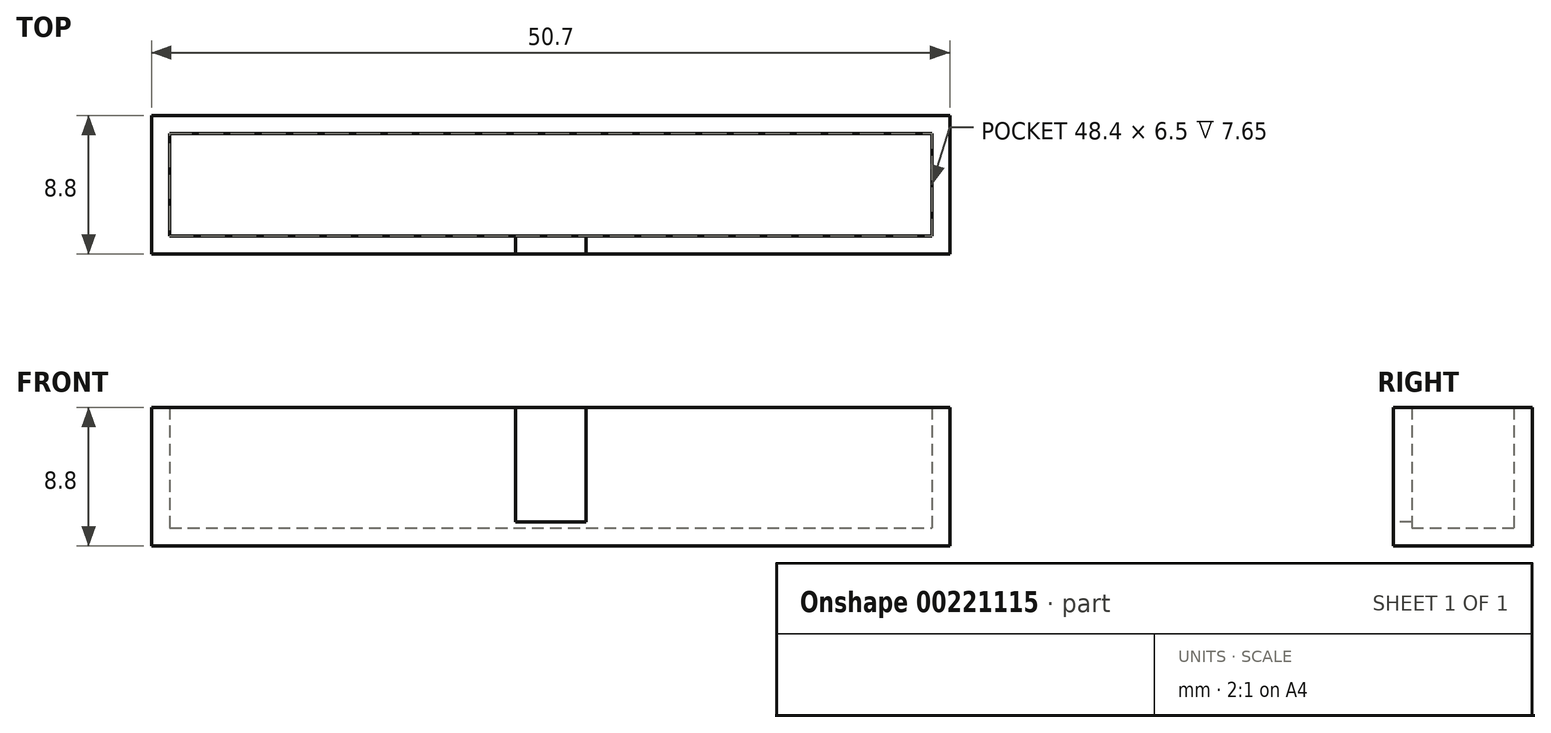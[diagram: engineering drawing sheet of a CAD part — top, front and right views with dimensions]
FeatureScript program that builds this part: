
annotation { "Feature Type Name" : "Feature", "Feature Type Description" : "" }
export const myFeature = defineFeature(function(context is Context, id is Id, definition is map)
    precondition{}
    {
        {
            var Q0;
            Q0=qCreatedBy(makeId("Top.planeOp"),FACE);
            var sketch = newSketch(context, id + "F0", { "sketchPlane" : qUnion([Q0])});
            skLineSegment(sketch, "E0.bottom", {"start": v(-25.35, 0) * mm, "end": v(25.35, 0) * mm});
            skLineSegment(sketch, "E0.top", {"start": v(-25.35, 8.8) * mm, "end": v(25.35, 8.8) * mm});
            skLineSegment(sketch, "E0.left", {"start": v(-25.35, 0) * mm, "end": v(-25.35, 8.8) * mm});
            skLineSegment(sketch, "E0.right", {"start": v(25.35, 0) * mm, "end": v(25.35, 8.8) * mm});
            skSolve(sketch);
        }
        {
            var Q0;
            Q0 = qSketchRegion(id + "F0", true);
            extrude(context, id + "F1", {"entities" : qUnion([Q0]), "depth" : 8.8 * mm});
        }
        {
            var Q0;
            Q0=makeQuery(id+"F1.opExtrude","CAP_FACE",FACE,{"disambiguationData":[OSD([sQuery(id+"F0.wireOp",EDGE,"E0.bottom"),sQuery(id+"F0.wireOp",EDGE,"E0.top"),sQuery(id+"F0.wireOp",EDGE,"E0.left"),sQuery(id+"F0.wireOp",EDGE,"E0.right")])],"isStart":false});
            shell(context, id + "F2", {"entities" : qUnion([Q0]), "thickness" : 1.15 * mm});
        }
        {
            var Q0;
            Q0=qCreatedBy(makeId("Front.planeOp"),FACE);
            var sketch = newSketch(context, id + "F3", { "sketchPlane" : qUnion([Q0])});
            skLineSegment(sketch, "E1.bottom", {"start": v(-2.25, 8.8) * mm, "end": v(2.25, 8.8) * mm});
            skLineSegment(sketch, "E1.top", {"start": v(-2.25, 1.54) * mm, "end": v(2.25, 1.54) * mm});
            skLineSegment(sketch, "E1.left", {"start": v(-2.25, 8.8) * mm, "end": v(-2.25, 1.54) * mm});
            skLineSegment(sketch, "E1.right", {"start": v(2.25, 8.8) * mm, "end": v(2.25, 1.54) * mm});
            skSolve(sketch);
        }
        {
            var Q0;
            Q0=makeQuery(id+"F3.imprint","IMPRINT",FACE,{"disambiguationData":[TD([[makeQuery(id+"F3.imprint","IMPRINT",EDGE,{"derivedFrom":sQuery(id+"F3.wireOp",EDGE,"E1.bottom")}),-1.0]])]});
            extrude(context, id + "F4", {"entities" : qUnion([Q0]), "operationType" : NewBodyOperationType.REMOVE, "oppositeDirection" : true, "depth" : 1.15 * mm});
        }
    });
